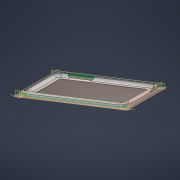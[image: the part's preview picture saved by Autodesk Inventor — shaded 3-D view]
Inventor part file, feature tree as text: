
AUTODESK INVENTOR PART (.ipt)
format: ipt  version: 2021 (Build 250183000, 183)  size: 253,440 bytes
history: native  units: mm
features: extrude x4, sketch x4, fillet x3, plane x2, thicken_offset x1
ambient origin geometry x8: Origin, YZ Plane, XZ Plane, XY Plane, X Axis, Y Axis, Z Axis, Center Point
bodies: Solid1 (feature_tree), Solid2 (feature_tree)
feature tree (14):
  extrude  "Extrusion1"  Depth=5.9mm
  fillet  "Fillet1"  [1 undecoded]
  fillet  "Fillet2"  Radius=9.9mm
  fillet  "Fillet3"  Radius=5.9mm
  thicken_offset  "Thicken1"
  extrude  "Extrusion2"  Depth=8.0mm
  plane  "Work Plane1"
  extrude  "Extrusion3"  Depth=8.0mm
  plane  "Work Plane2"
  extrude  "Extrusion5"  Depth=5.9mm
  sketch  "Sketch1"  dims[d0=208.4mm d1=137.5mm d3=0.0mm d4=9.9mm d6=5.9mm]
  sketch  "Sketch3"  dims[d7=0.98mm d8=0.8mm d14=8.0mm]
  sketch  "Sketch4"  dims[d15=8.0mm d17=8.0mm]
  sketch  "Sketch5"  dims[d18=0.0mm d19=0.0mm d20=53.5mm d21=24.5mm d22=10.0mm d23=0.0mm d24=19.0mm d25=19.0mm d28=5.9mm d29=10.0mm d30=0.0mm d31=5.9mm]
note: 1 required parameter value undecoded (feature->parameter linkage not recoverable at this tier; creation-order binding heuristic only, values carry confidence <= 0.55)
